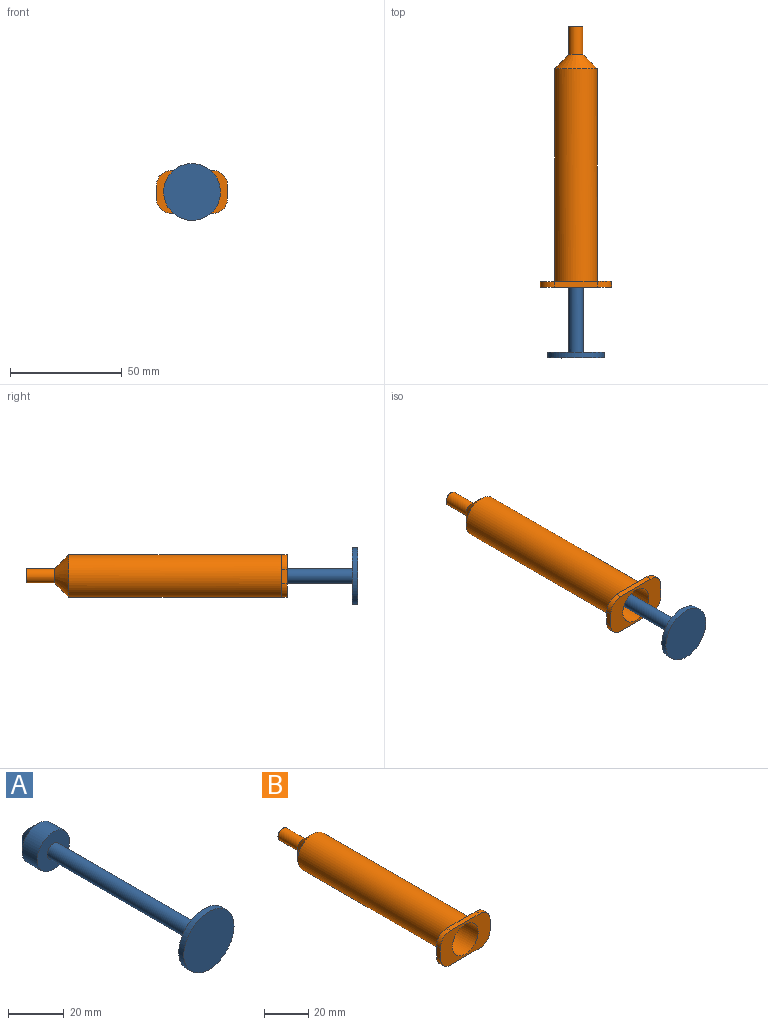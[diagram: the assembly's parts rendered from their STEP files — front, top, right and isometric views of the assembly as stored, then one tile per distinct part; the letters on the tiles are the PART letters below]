
ASSEMBLY  parts=2 mates=1
PART A: 8 faces, bbox 25.4x91.4x25.4 mm
  f0: cylinder r=8.26mm len=16.51mm, axis (0,1,0), area 395.2mm2, adj f1,f7
  f1: plane 16.51x16.51mm, normal (0,-1,0), area 182.4mm2, adj f0,f3
  f2: plane 6.35x6.35mm, normal (0,1,0), area 31.7mm2, adj f7
  f3: cylinder r=3.17mm len=76.2mm, axis (0,1,0), area 1520.1mm2, adj f1,f6
  f4: cylinder r=12.7mm len=25.4mm, axis (0,1,0), area 202.7mm2, adj f5,f6
  f5: plane 25.4x25.4mm, normal (0,-1,0), area 506.7mm2, adj f4
  f6: plane 25.4x25.4mm, normal (0,1,0), area 475mm2, adj f3,f4
  f7: cone r=8.26mm half-angle=45deg, axis (0,-1,0), area 258mm2, adj f0,f2
PART B: 18 faces, bbox 31.8x116.8x19.1 mm
  f0: cylinder r=9.53mm len=95.25mm, axis (0,-1,0), area 5700.5mm2, adj f1,f7,f8
  f1: cone r=9.53mm half-angle=45deg, axis (0,-1,0), area 358.3mm2, adj f0,f2
  f2: cylinder r=3.17mm len=12.7mm, axis (0,-1,0), area 253.4mm2, adj f1,f3
  f3: plane 6.35x6.35mm, normal (0,1,0), area 20.3mm2, adj f2,f6
  f4: cylinder r=8.26mm len=97.26mm, axis (0,-1,0), area 5044.9mm2, adj f5,f13
  f5: cone r=8.63mm half-angle=45deg, axis (0,-1,0), area 286.6mm2, adj f4,f6
  f6: cylinder r=1.91mm len=13.23mm, axis (0,-1,0), area 158.3mm2, adj f3,f5
  f7: plane 19.05x15.88mm, normal (0,1,0), area 142.6mm2, adj f0,f9,f10,f12,f14,f15
  f8: plane 19.05x15.88mm, normal (0,1,0), area 142.6mm2, adj f0,f10,f11,f12,f16,f17
  f9: plane 6.35x2.54mm, normal (-1,0,0), area 16.1mm2, adj f7,f13,f14,f15
  f10: plane 19.05x2.54mm, normal (0,0,-1), area 48.4mm2, adj f7,f8,f13,f14,f16
  f11: plane 6.35x2.54mm, normal (1,0,0), area 16.1mm2, adj f8,f13,f16,f17
  f12: plane 19.05x2.54mm, normal (0,0,1), area 48.4mm2, adj f7,f8,f13,f15,f17
  f13: plane 31.75x19.05mm, normal (0,-1,0), area 356.1mm2, adj f4,f9,f10,f11,f12,f14,f15,f16
  f14: cylinder r=6.35mm len=6.35mm, axis (0,1,0), area 25.3mm2, adj f7,f9,f10,f13
  f15: cylinder r=6.35mm len=6.35mm, axis (0,-1,0), area 25.3mm2, adj f7,f9,f12,f13
  f16: cylinder r=6.35mm len=6.35mm, axis (0,-1,0), area 25.3mm2, adj f8,f10,f11,f13
  f17: cylinder r=6.35mm len=6.35mm, axis (0,1,0), area 25.3mm2, adj f8,f11,f12,f13
PLACE A rot(axis=(0.09,-0.98,0.16),0.3deg) t=(132.61,-44.67,48.11)mm
PLACE B rot(axis=(0.09,-0.98,0.16),0.3deg) t=(178.38,-101.88,46.09)mm
MATE cylindrical A.f0 <-> B.f0  axis (0,1,0) through (154.83,-53.55,63.13)mm
